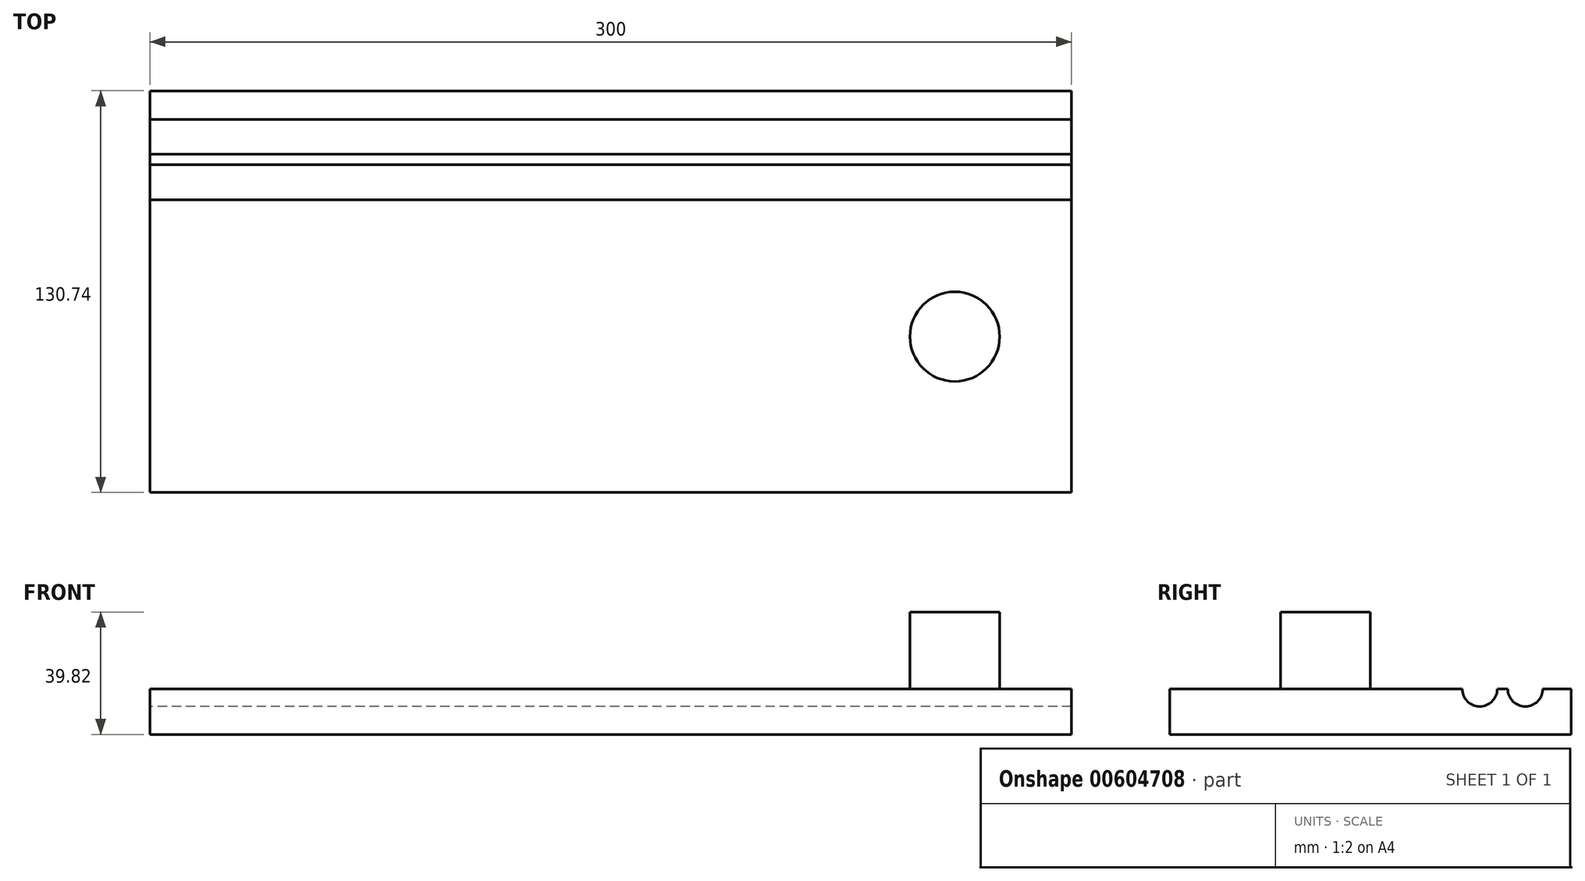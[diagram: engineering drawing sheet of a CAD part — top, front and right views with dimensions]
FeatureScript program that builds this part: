
annotation { "Feature Type Name" : "Feature", "Feature Type Description" : "" }
export const myFeature = defineFeature(function(context is Context, id is Id, definition is map)
    precondition{}
    {
        {
            var Q0;
            Q0=qCreatedBy(makeId("Right.planeOp"),FACE);
            var sketch = newSketch(context, id + "F0", { "sketchPlane" : qUnion([Q0])});
            skLineSegment(sketch, "E0.bottom", {"start": v(-65.37, 7.41) * mm, "end": v(29.86, 7.41) * mm});
            skLineSegment(sketch, "E0.top", {"start": v(-65.37, -7.41) * mm, "end": v(65.37, -7.41) * mm});
            skLineSegment(sketch, "E0.left", {"start": v(-65.37, 7.41) * mm, "end": v(-65.37, -7.41) * mm});
            skLineSegment(sketch, "E0.right", {"start": v(65.37, 7.41) * mm, "end": v(65.37, -7.41) * mm});
            skPoint(sketch, "E0.middle", {"position": v(0, 0) * mm});
            skArc(sketch, "E1", {"start": v(44.67, 7.41) * mm, "mid": v(50.38, 1.7) * mm, "end": v(56.1, 7.41) * mm});
            skArc(sketch, "E2", {"start": v(29.86, 7.41) * mm, "mid": v(35.57, 1.7) * mm, "end": v(41.28, 7.41) * mm});
            skLineSegment(sketch, "E3.trimOffspring", {"start": v(56.1, 7.41) * mm, "end": v(65.37, 7.41) * mm});
            skLineSegment(sketch, "E4.trimOffspring", {"start": v(41.28, 7.41) * mm, "end": v(44.67, 7.41) * mm});
            skSolve(sketch);
        }
        {
            var Q0;
            Q0=makeQuery(id+"F0.imprint","IMPRINT",FACE,{"disambiguationData":[TD([[makeQuery(id+"F0.imprint","IMPRINT",EDGE,{"derivedFrom":sQuery(id+"F0.wireOp",EDGE,"E0.bottom")}),-1.0]])]});
            extrude(context, id + "F1", {"entities" : qUnion([Q0]), "depth" : 300 * mm, "offsetDistance" : 25 * mm});
        }
        {
            var Q0;
            Q0=makeQuery(id+"F1.opExtrude","SWEPT_FACE",FACE,{"disambiguationData":[OSD([sQuery(id+"F0.wireOp",EDGE,"E0.bottom")])]});
            var sketch = newSketch(context, id + "F2", { "sketchPlane" : qUnion([Q0])});
            skCircle(sketch, "E5", {"center": v(262.05, -14.66) * mm, "radius": 14.6 * mm});
            skSolve(sketch);
        }
        {
            var Q0;
            Q0=makeQuery(id+"F2.imprint","IMPRINT",FACE,{"disambiguationData":[TD([[makeQuery(id+"F2.imprint","IMPRINT",EDGE,{"derivedFrom":sQuery(id+"F2.wireOp",EDGE,"E5")}),1.0]])]});
            extrude(context, id + "F3", {"entities" : qUnion([Q0]), "operationType" : NewBodyOperationType.ADD, "depth" : 25 * mm, "offsetDistance" : 25 * mm});
        }
    });
